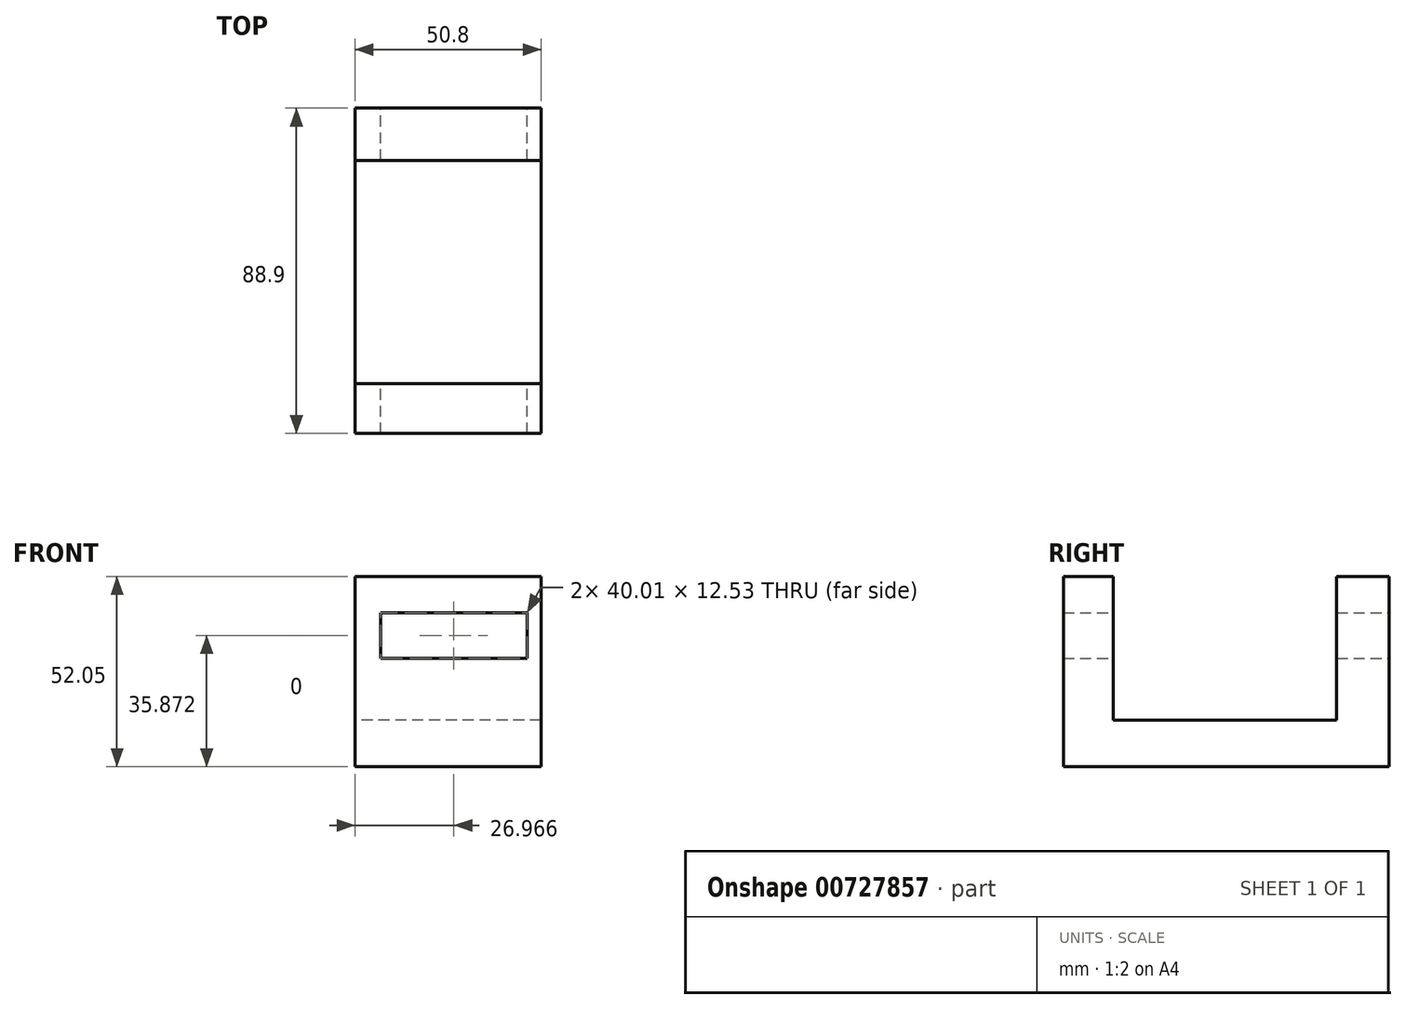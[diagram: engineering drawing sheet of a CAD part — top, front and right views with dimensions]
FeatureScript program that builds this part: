
annotation { "Feature Type Name" : "Feature", "Feature Type Description" : "" }
export const myFeature = defineFeature(function(context is Context, id is Id, definition is map)
    precondition{}
    {
        {
            var Q0;
            Q0=qCreatedBy(makeId("Right.planeOp"),FACE);
            var sketch = newSketch(context, id + "F0", { "sketchPlane" : qUnion([Q0])});
            skLineSegment(sketch, "E0.bottom", {"start": v(46.9, 6.35) * mm, "end": v(-42, 6.35) * mm});
            skLineSegment(sketch, "E0.top", {"start": v(46.9, -6.35) * mm, "end": v(-42, -6.35) * mm});
            skLineSegment(sketch, "E0.left", {"start": v(46.9, 6.35) * mm, "end": v(46.9, -6.35) * mm});
            skLineSegment(sketch, "E0.right", {"start": v(-42, 6.35) * mm, "end": v(-42, -6.35) * mm});
            skPoint(sketch, "E0.middle", {"position": v(2.44, 0) * mm});
            skLineSegment(sketch, "E1.bottom", {"start": v(-42, -6.35) * mm, "end": v(-28.32, -6.35) * mm});
            skLineSegment(sketch, "E1.top", {"start": v(-42, 45.7) * mm, "end": v(-28.32, 45.7) * mm});
            skLineSegment(sketch, "E1.left", {"start": v(-42, -6.35) * mm, "end": v(-42, 45.7) * mm});
            skLineSegment(sketch, "E1.right", {"start": v(-28.32, -6.35) * mm, "end": v(-28.32, 45.7) * mm});
            skLineSegment(sketch, "E2.bottom", {"start": v(46.9, -6.35) * mm, "end": v(32.66, -6.35) * mm});
            skLineSegment(sketch, "E2.top", {"start": v(46.9, 45.7) * mm, "end": v(32.66, 45.7) * mm});
            skLineSegment(sketch, "E2.left", {"start": v(46.9, -6.35) * mm, "end": v(46.9, 45.7) * mm});
            skLineSegment(sketch, "E2.right", {"start": v(32.66, -6.35) * mm, "end": v(32.66, 45.7) * mm});
            skSolve(sketch);
        }
        {
            var Q0;
            {var subQ5=sQuery(id+"F0.wireOp",EDGE,"E1.top");Q0=makeQuery(id+"F0.imprint","IMPRINT",FACE,{"disambiguationData":[TD([[makeQuery(id+"F0.imprint","IMPRINT",EDGE,{"derivedFrom":subQ5}),-1.0]])]});}
            var Q1;
            {var subQ5=sQuery(id+"F0.wireOp",EDGE,"E1.bottom");Q1=makeQuery(id+"F0.imprint","IMPRINT",FACE,{"disambiguationData":[TD([[makeQuery(id+"F0.imprint","IMPRINT",EDGE,{"derivedFrom":subQ5}),1.0]])]});}
            var Q2;
            {var subQ5=sQuery(id+"F0.wireOp",EDGE,"E0.top");Q2=makeQuery(id+"F0.imprint","IMPRINT",FACE,{"disambiguationData":[TD([[makeQuery(id+"F0.imprint","IMPRINT",EDGE,{"derivedFrom":subQ5}),-1.0]])]});}
            var Q3;
            {var subQ5=sQuery(id+"F0.wireOp",EDGE,"E2.bottom");Q3=makeQuery(id+"F0.imprint","IMPRINT",FACE,{"disambiguationData":[TD([[makeQuery(id+"F0.imprint","IMPRINT",EDGE,{"derivedFrom":subQ5}),-1.0]])]});}
            var Q4;
            {var subQ5=sQuery(id+"F0.wireOp",EDGE,"E2.top");Q4=makeQuery(id+"F0.imprint","IMPRINT",FACE,{"disambiguationData":[TD([[makeQuery(id+"F0.imprint","IMPRINT",EDGE,{"derivedFrom":subQ5}),1.0]])]});}
            extrude(context, id + "F1", {"entities" : qUnion([Q0, Q1, Q2, Q3, Q4]), "depth" : 50.8 * mm, "offsetDistance" : 25.4 * mm});
        }
        {
            var Q0;
            Q0=makeQuery(id+"F1.opExtrude","SWEPT_FACE",FACE,{"disambiguationData":[OSD([sQuery(id+"F0.wireOp",EDGE,"E2.left")])]});
            var sketch = newSketch(context, id + "F2", { "sketchPlane" : qUnion([Q0])});
            skLineSegment(sketch, "E3.bottom", {"start": v(-36.37, 23.26) * mm, "end": v(-6.96, 23.26) * mm});
            skLineSegment(sketch, "E3.top", {"start": v(-36.37, 35.79) * mm, "end": v(-6.96, 35.79) * mm});
            skLineSegment(sketch, "E3.right", {"start": v(-6.96, 23.26) * mm, "end": v(-6.96, 35.79) * mm});
            skLineSegment(sketch, "E4.bottom", {"start": v(-36.37, 35.79) * mm, "end": v(-46.97, 35.79) * mm});
            skLineSegment(sketch, "E4.top", {"start": v(-36.37, 23.26) * mm, "end": v(-46.97, 23.26) * mm});
            skLineSegment(sketch, "E4.right", {"start": v(-46.97, 35.79) * mm, "end": v(-46.97, 23.26) * mm});
            skSolve(sketch);
        }
        {
            var Q0;
            Q0=makeQuery(id+"F2.imprint","IMPRINT",FACE,{"disambiguationData":[TD([[makeQuery(id+"F2.imprint","IMPRINT",EDGE,{"derivedFrom":sQuery(id+"F2.wireOp",EDGE,"E3.bottom")}),1.0]])]});
            extrude(context, id + "F3", {"entities" : qUnion([Q0]), "operationType" : NewBodyOperationType.REMOVE, "endBound" : BoundingType.THROUGH_ALL, "oppositeDirection" : true, "depth" : 25.4 * mm, "offsetDistance" : 25.4 * mm});
        }
    });
